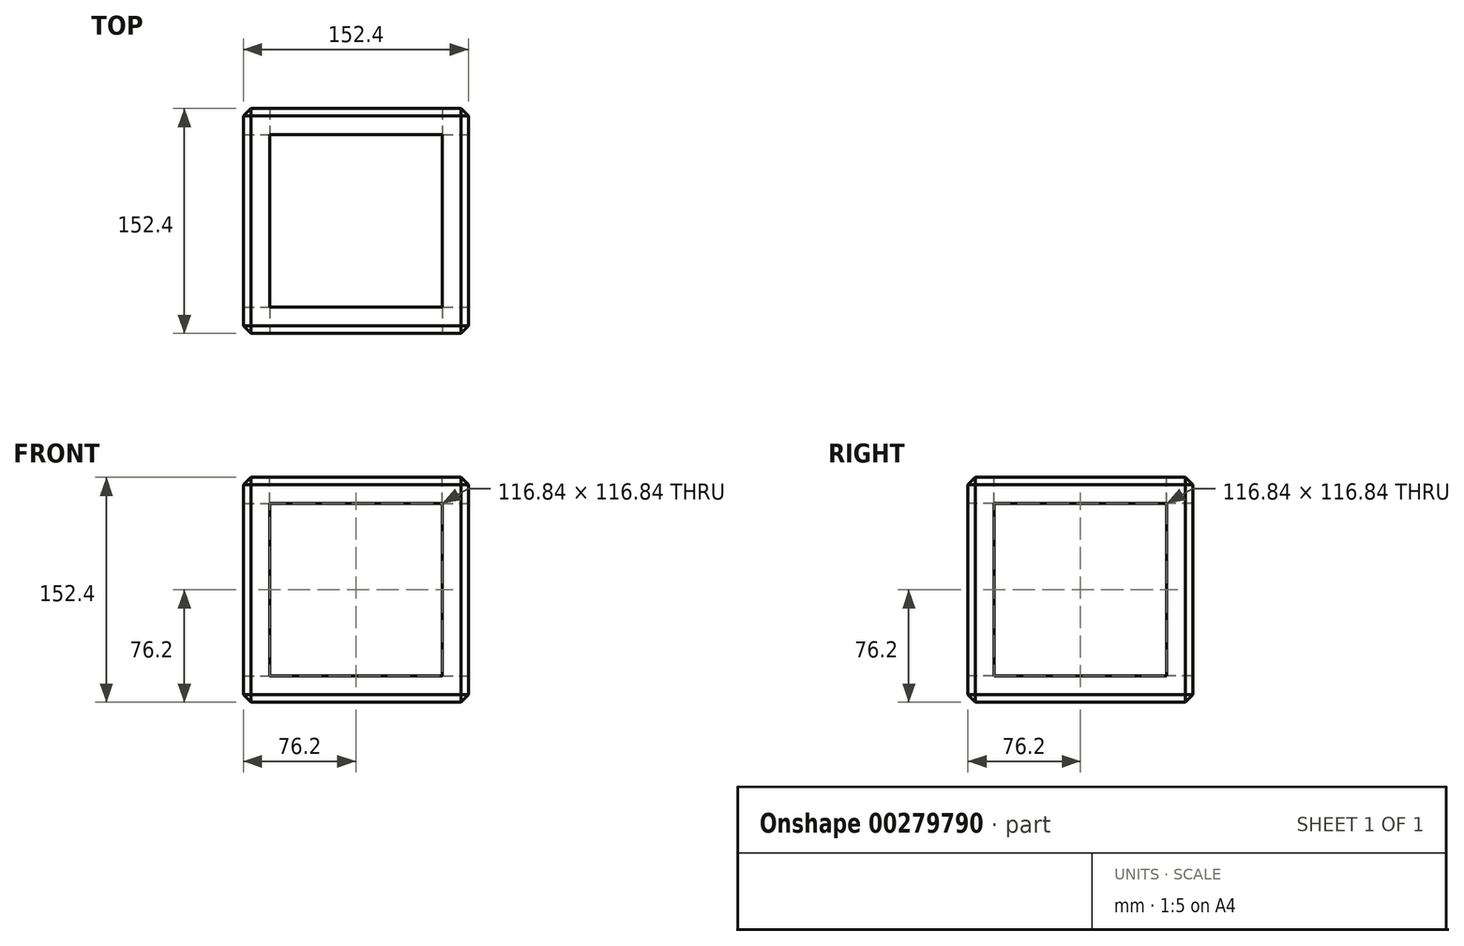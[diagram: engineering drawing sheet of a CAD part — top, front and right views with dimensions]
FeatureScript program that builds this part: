
annotation { "Feature Type Name" : "Feature", "Feature Type Description" : "" }
export const myFeature = defineFeature(function(context is Context, id is Id, definition is map)
    precondition{}
    {
        {
            var Q0;
            Q0=qCreatedBy(makeId("Top.planeOp"),FACE);
            var sketch = newSketch(context, id + "F0", { "sketchPlane" : qUnion([Q0])});
            skLineSegment(sketch, "E0.bottom", {"start": v(0, 0) * mm, "end": v(-152.4, 0) * mm});
            skLineSegment(sketch, "E0.top", {"start": v(0, 152.4) * mm, "end": v(-152.4, 152.4) * mm});
            skLineSegment(sketch, "E0.left", {"start": v(0, 0) * mm, "end": v(0, 152.4) * mm});
            skLineSegment(sketch, "E0.right", {"start": v(-152.4, 0) * mm, "end": v(-152.4, 152.4) * mm});
            skSolve(sketch);
        }
        {
            var Q0;
            Q0=makeQuery(id+"F0.imprint","IMPRINT",FACE,{"disambiguationData":[TD([[makeQuery(id+"F0.imprint","IMPRINT",EDGE,{"derivedFrom":sQuery(id+"F0.wireOp",EDGE,"E0.bottom")}),-1.0]])]});
            extrude(context, id + "F1", {"entities" : qUnion([Q0]), "depth" : 152.4 * mm});
        }
        {
            var Q0;
            Q0=makeQuery(id+"F1.opExtrude","SWEPT_FACE",FACE,{"disambiguationData":[OSD([sQuery(id+"F0.wireOp",EDGE,"E0.bottom")])]});
            var sketch = newSketch(context, id + "F2", { "sketchPlane" : qUnion([Q0])});
            skLineSegment(sketch, "E1.bottom", {"start": v(-134.62, 134.62) * mm, "end": v(-17.78, 134.62) * mm});
            skLineSegment(sketch, "E1.top", {"start": v(-134.62, 17.78) * mm, "end": v(-17.78, 17.78) * mm});
            skLineSegment(sketch, "E1.left", {"start": v(-134.62, 134.62) * mm, "end": v(-134.62, 17.78) * mm});
            skLineSegment(sketch, "E1.right", {"start": v(-17.78, 134.62) * mm, "end": v(-17.78, 17.78) * mm});
            skSolve(sketch);
        }
        {
            var Q0;
            Q0=makeQuery(id+"F2.imprint","IMPRINT",FACE,{"disambiguationData":[TD([[makeQuery(id+"F2.imprint","IMPRINT",EDGE,{"derivedFrom":sQuery(id+"F2.wireOp",EDGE,"E1.bottom")}),-1.0]])]});
            extrude(context, id + "F3", {"entities" : qUnion([Q0]), "operationType" : NewBodyOperationType.REMOVE, "endBound" : BoundingType.THROUGH_ALL, "oppositeDirection" : true, "depth" : 152.4 * mm});
        }
        {
            var Q0;
            Q0=makeQuery(id+"F1.opExtrude","SWEPT_FACE",FACE,{"disambiguationData":[OSD([sQuery(id+"F0.wireOp",EDGE,"E0.left")])]});
            var sketch = newSketch(context, id + "F4", { "sketchPlane" : qUnion([Q0])});
            skLineSegment(sketch, "E2.bottom", {"start": v(17.78, 134.62) * mm, "end": v(134.62, 134.62) * mm});
            skLineSegment(sketch, "E2.top", {"start": v(17.78, 17.78) * mm, "end": v(134.62, 17.78) * mm});
            skLineSegment(sketch, "E2.left", {"start": v(17.78, 134.62) * mm, "end": v(17.78, 17.78) * mm});
            skLineSegment(sketch, "E2.right", {"start": v(134.62, 134.62) * mm, "end": v(134.62, 17.78) * mm});
            skSolve(sketch);
        }
        {
            var Q0;
            Q0=makeQuery(id+"F4.imprint","IMPRINT",FACE,{"disambiguationData":[TD([[makeQuery(id+"F4.imprint","IMPRINT",EDGE,{"derivedFrom":sQuery(id+"F4.wireOp",EDGE,"E2.bottom")}),-1.0]])]});
            extrude(context, id + "F5", {"entities" : qUnion([Q0]), "operationType" : NewBodyOperationType.REMOVE, "endBound" : BoundingType.THROUGH_ALL, "oppositeDirection" : true, "depth" : 25.4 * mm});
        }
        {
            var Q0;
            Q0=makeQuery(id+"F1.opExtrude","CAP_FACE",FACE,{"disambiguationData":[OSD([sQuery(id+"F0.wireOp",EDGE,"E0.bottom"),sQuery(id+"F0.wireOp",EDGE,"E0.top"),sQuery(id+"F0.wireOp",EDGE,"E0.left"),sQuery(id+"F0.wireOp",EDGE,"E0.right")])],"isStart":false});
            var sketch = newSketch(context, id + "F6", { "sketchPlane" : qUnion([Q0])});
            skLineSegment(sketch, "E3.bottom", {"start": v(-134.62, 134.62) * mm, "end": v(-17.78, 134.62) * mm});
            skLineSegment(sketch, "E3.top", {"start": v(-134.62, 17.78) * mm, "end": v(-17.78, 17.78) * mm});
            skLineSegment(sketch, "E3.left", {"start": v(-134.62, 134.62) * mm, "end": v(-134.62, 17.78) * mm});
            skLineSegment(sketch, "E3.right", {"start": v(-17.78, 134.62) * mm, "end": v(-17.78, 17.78) * mm});
            skSolve(sketch);
        }
        {
            var Q0;
            Q0=makeQuery(id+"F6.imprint","IMPRINT",FACE,{"disambiguationData":[TD([[makeQuery(id+"F6.imprint","IMPRINT",EDGE,{"derivedFrom":sQuery(id+"F6.wireOp",EDGE,"E3.bottom")}),-1.0]])]});
            extrude(context, id + "F7", {"entities" : qUnion([Q0]), "operationType" : NewBodyOperationType.REMOVE, "oppositeDirection" : true, "depth" : 17.78 * mm});
        }
        {
            var Q0;
            Q0=makeQuery(id+"F1.opExtrude","CAP_EDGE",EDGE,{"disambiguationData":[OSD([sQuery(id+"F0.wireOp",EDGE,"E0.bottom")])],"isStart":false});
            var Q1;
            Q1=makeQuery(id+"F1.opExtrude","CAP_EDGE",EDGE,{"disambiguationData":[OSD([sQuery(id+"F0.wireOp",EDGE,"E0.left")])],"isStart":false});
            var Q2;
            Q2=makeQuery(id+"F1.opExtrude","SWEPT_EDGE",EDGE,{"disambiguationData":[OSD([sQuery(id+"F0.wireOp",EDGE,"E0.bottom"),sQuery(id+"F0.wireOp",EDGE,"E0.left")])]});
            var Q3;
            Q3=makeQuery(id+"F1.opExtrude","CAP_EDGE",EDGE,{"disambiguationData":[OSD([sQuery(id+"F0.wireOp",EDGE,"E0.top")])],"isStart":false});
            var Q4;
            Q4=makeQuery(id+"F1.opExtrude","CAP_EDGE",EDGE,{"disambiguationData":[OSD([sQuery(id+"F0.wireOp",EDGE,"E0.right")])],"isStart":false});
            var Q5;
            Q5=makeQuery(id+"F1.opExtrude","SWEPT_EDGE",EDGE,{"disambiguationData":[OSD([sQuery(id+"F0.wireOp",EDGE,"E0.top"),sQuery(id+"F0.wireOp",EDGE,"E0.left")])]});
            var Q6;
            Q6=makeQuery(id+"F1.opExtrude","SWEPT_EDGE",EDGE,{"disambiguationData":[OSD([sQuery(id+"F0.wireOp",EDGE,"E0.top"),sQuery(id+"F0.wireOp",EDGE,"E0.right")])]});
            var Q7;
            Q7=makeQuery(id+"F1.opExtrude","SWEPT_EDGE",EDGE,{"disambiguationData":[OSD([sQuery(id+"F0.wireOp",EDGE,"E0.bottom"),sQuery(id+"F0.wireOp",EDGE,"E0.right")])]});
            var Q8;
            Q8=makeQuery(id+"F1.opExtrude","CAP_FACE",FACE,{"disambiguationData":[OSD([sQuery(id+"F0.wireOp",EDGE,"E0.bottom"),sQuery(id+"F0.wireOp",EDGE,"E0.top"),sQuery(id+"F0.wireOp",EDGE,"E0.left"),sQuery(id+"F0.wireOp",EDGE,"E0.right")])],"isStart":true});
            chamfer(context, id + "F8", {"entities" : qUnion([Q0, Q1, Q2, Q3, Q4, Q5, Q6, Q7, Q8]), "width" : 5.08 * mm, "tangentPropagation" : true});
        }
    });
